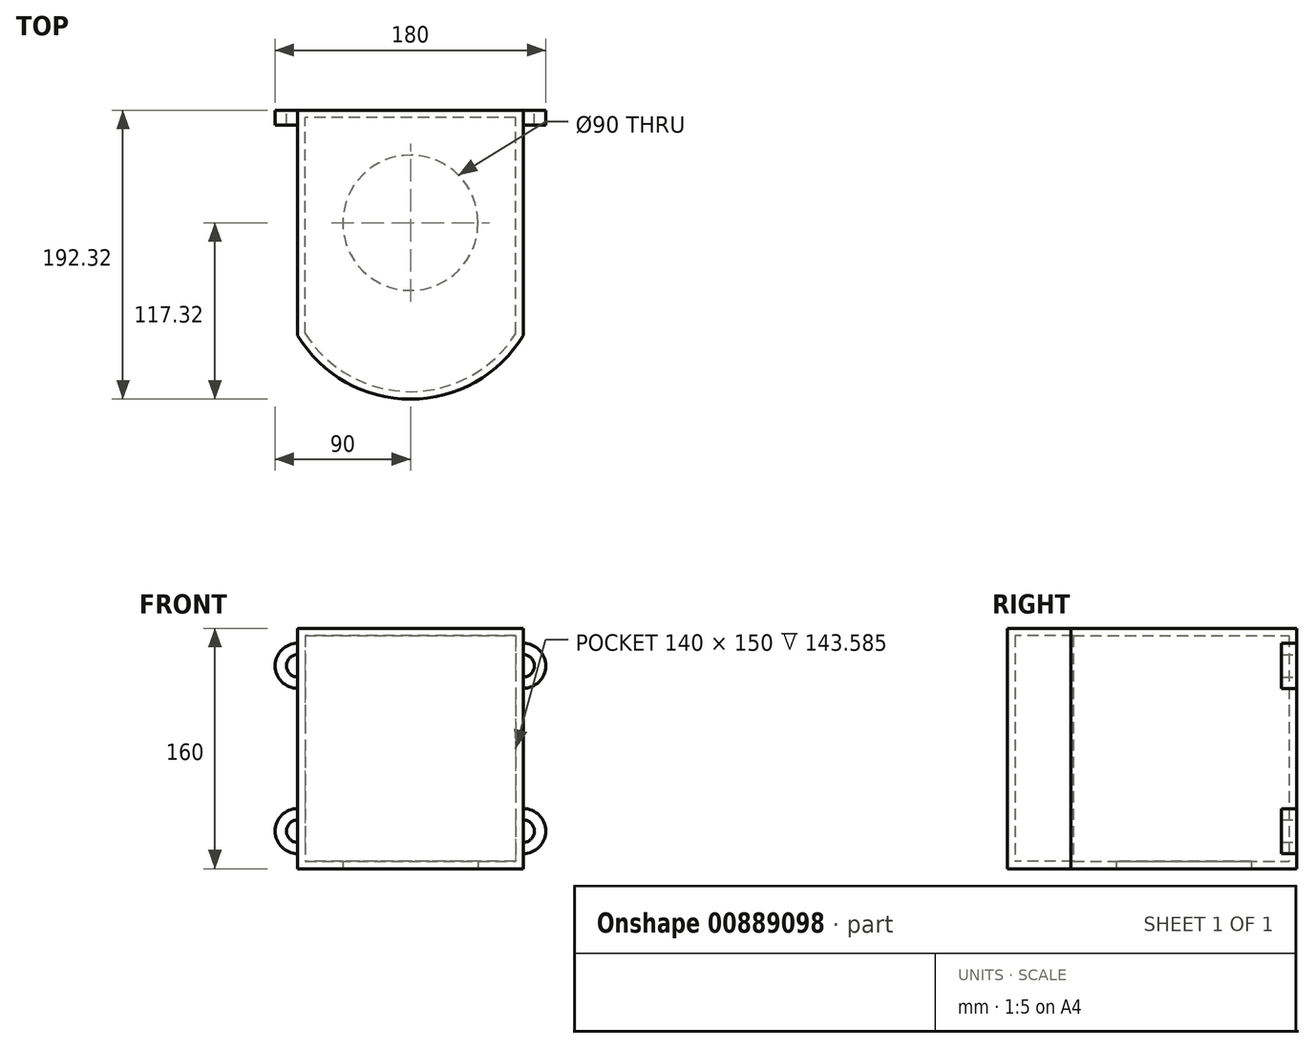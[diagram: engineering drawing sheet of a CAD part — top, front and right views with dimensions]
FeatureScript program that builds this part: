
annotation { "Feature Type Name" : "Feature", "Feature Type Description" : "" }
export const myFeature = defineFeature(function(context is Context, id is Id, definition is map)
    precondition{}
    {
        {
            var Q0;
            Q0=qCreatedBy(makeId("Top.planeOp"),FACE);
            var sketch = newSketch(context, id + "F0", { "sketchPlane" : qUnion([Q0])});
            skCircle(sketch, "E0", {"center": v(0, 0) * mm, "radius": 45 * mm});
            skLineSegment(sketch, "E1.top", {"start": v(75, 75) * mm, "end": v(-75, 75) * mm});
            skLineSegment(sketch, "E1.left", {"start": v(75, -75) * mm, "end": v(75, 75) * mm});
            skLineSegment(sketch, "E1.right", {"start": v(-75, -75) * mm, "end": v(-75, 75) * mm});
            skArc(sketch, "E2", {"start": v(-75, -75) * mm, "mid": v(0, -117.32) * mm, "end": v(75, -75) * mm});
            skSolve(sketch);
        }
        {
            var Q0;
            Q0=makeQuery(id+"F0.imprint","IMPRINT",FACE,{"disambiguationData":[TD([[makeQuery(id+"F0.imprint","IMPRINT",EDGE,{"derivedFrom":sQuery(id+"F0.wireOp",EDGE,"E0")}),-1.0]])]});
            var Q1;
            Q1=makeQuery(id+"F0.imprint","IMPRINT",FACE,{"disambiguationData":[TD([[makeQuery(id+"F0.imprint","IMPRINT",EDGE,{"derivedFrom":sQuery(id+"F0.wireOp",EDGE,"E0")}),1.0]])]});
            extrude(context, id + "F1", {"entities" : qUnion([Q0, Q1]), "depth" : 160 * mm, "offsetDistance" : 25 * mm});
        }
        {
            var Q0;
            Q0=makeQuery(id+"F1.opExtrude","CAP_FACE",FACE,{"disambiguationData":[OSD([sQuery(id+"F0.wireOp",EDGE,"E1.top"),sQuery(id+"F0.wireOp",EDGE,"E1.left"),sQuery(id+"F0.wireOp",EDGE,"E1.right"),sQuery(id+"F0.wireOp",EDGE,"E2")])],"isStart":true});
            shell(context, id + "F2", {"entities" : qUnion([Q0]), "thickness" : 5 * mm});
        }
        {
            var Q0;
            Q0=makeQuery(id+"F0.imprint","IMPRINT",FACE,{"disambiguationData":[TD([[makeQuery(id+"F0.imprint","IMPRINT",EDGE,{"derivedFrom":sQuery(id+"F0.wireOp",EDGE,"E0")}),-1.0]])]});
            extrude(context, id + "F3", {"entities" : qUnion([Q0]), "operationType" : NewBodyOperationType.ADD, "depth" : 5 * mm, "offsetDistance" : 25 * mm});
        }
        {
            var Q0;
            Q0=makeQuery(id+"F1.opExtrude","SWEPT_FACE",FACE,{"disambiguationData":[OSD([sQuery(id+"F0.wireOp",EDGE,"E1.top")])]});
            var sketch = newSketch(context, id + "F4", { "sketchPlane" : qUnion([Q0])});
            skLineSegment(sketch, "E3", {"start": v(75, 0) * mm, "end": v(75, 25) * mm, "construction": true});
            skLineSegment(sketch, "E4", {"start": v(75, 25) * mm, "end": v(-75, 25) * mm, "construction": true});
            skLineSegment(sketch, "E5", {"start": v(75, 160) * mm, "end": v(75, 135) * mm, "construction": true});
            skLineSegment(sketch, "E6", {"start": v(-75, 135) * mm, "end": v(75, 135) * mm, "construction": true});
            skArc(sketch, "E7", {"start": v(75, 10) * mm, "mid": v(90, 25) * mm, "end": v(75, 40) * mm});
            skArc(sketch, "E8", {"start": v(-75, 40) * mm, "mid": v(-90, 25) * mm, "end": v(-75, 10) * mm});
            skArc(sketch, "E9", {"start": v(-75, 150) * mm, "mid": v(-90, 135) * mm, "end": v(-75, 120) * mm});
            skArc(sketch, "E10", {"start": v(75, 120) * mm, "mid": v(90, 135) * mm, "end": v(75, 150) * mm});
            skArc(sketch, "E11", {"start": v(75, 17.5) * mm, "mid": v(82.5, 25) * mm, "end": v(75, 32.5) * mm});
            skArc(sketch, "E12", {"start": v(-75, 32.5) * mm, "mid": v(-82.5, 25) * mm, "end": v(-75, 17.5) * mm});
            skArc(sketch, "E13", {"start": v(-75, 142.5) * mm, "mid": v(-82.5, 135) * mm, "end": v(-75, 127.5) * mm});
            skArc(sketch, "E14", {"start": v(75, 127.5) * mm, "mid": v(82.5, 135) * mm, "end": v(75, 142.5) * mm});
            skLineSegment(sketch, "E15", {"start": v(75, 0) * mm, "end": v(75, 160) * mm, "construction": true});
            skLineSegment(sketch, "E16", {"start": v(-75, 160) * mm, "end": v(-75, 0) * mm, "construction": true});
            skSolve(sketch);
        }
        {
            var Q0;
            Q0 = qSketchRegion(id + "F4", true);
            var Q1;
            {var subQ0=sQuery(id+"F4.wireOp",EDGE,"E9");Q1=makeQuery(id+"F4.imprint","IMPRINT",FACE,{"disambiguationData":[TD([[makeQuery(id+"F4.imprint","IMPRINT",EDGE,{"derivedFrom":subQ0}),1.0]])]});}
            var Q2;
            {var subQ0=sQuery(id+"F4.wireOp",EDGE,"E10");Q2=makeQuery(id+"F4.imprint","IMPRINT",FACE,{"disambiguationData":[TD([[makeQuery(id+"F4.imprint","IMPRINT",EDGE,{"derivedFrom":subQ0}),1.0]])]});}
            var Q3;
            {var subQ0=sQuery(id+"F4.wireOp",EDGE,"E8");Q3=makeQuery(id+"F4.imprint","IMPRINT",FACE,{"disambiguationData":[TD([[makeQuery(id+"F4.imprint","IMPRINT",EDGE,{"derivedFrom":subQ0}),1.0]])]});}
            var Q4;
            {var subQ0=sQuery(id+"F4.wireOp",EDGE,"E7");Q4=makeQuery(id+"F4.imprint","IMPRINT",FACE,{"disambiguationData":[TD([[makeQuery(id+"F4.imprint","IMPRINT",EDGE,{"derivedFrom":subQ0}),1.0]])]});}
            extrude(context, id + "F5", {"entities" : qUnion([Q0, Q1, Q2, Q3, Q4]), "operationType" : NewBodyOperationType.ADD, "oppositeDirection" : true, "depth" : 10 * mm, "offsetDistance" : 25 * mm});
        }
    });
